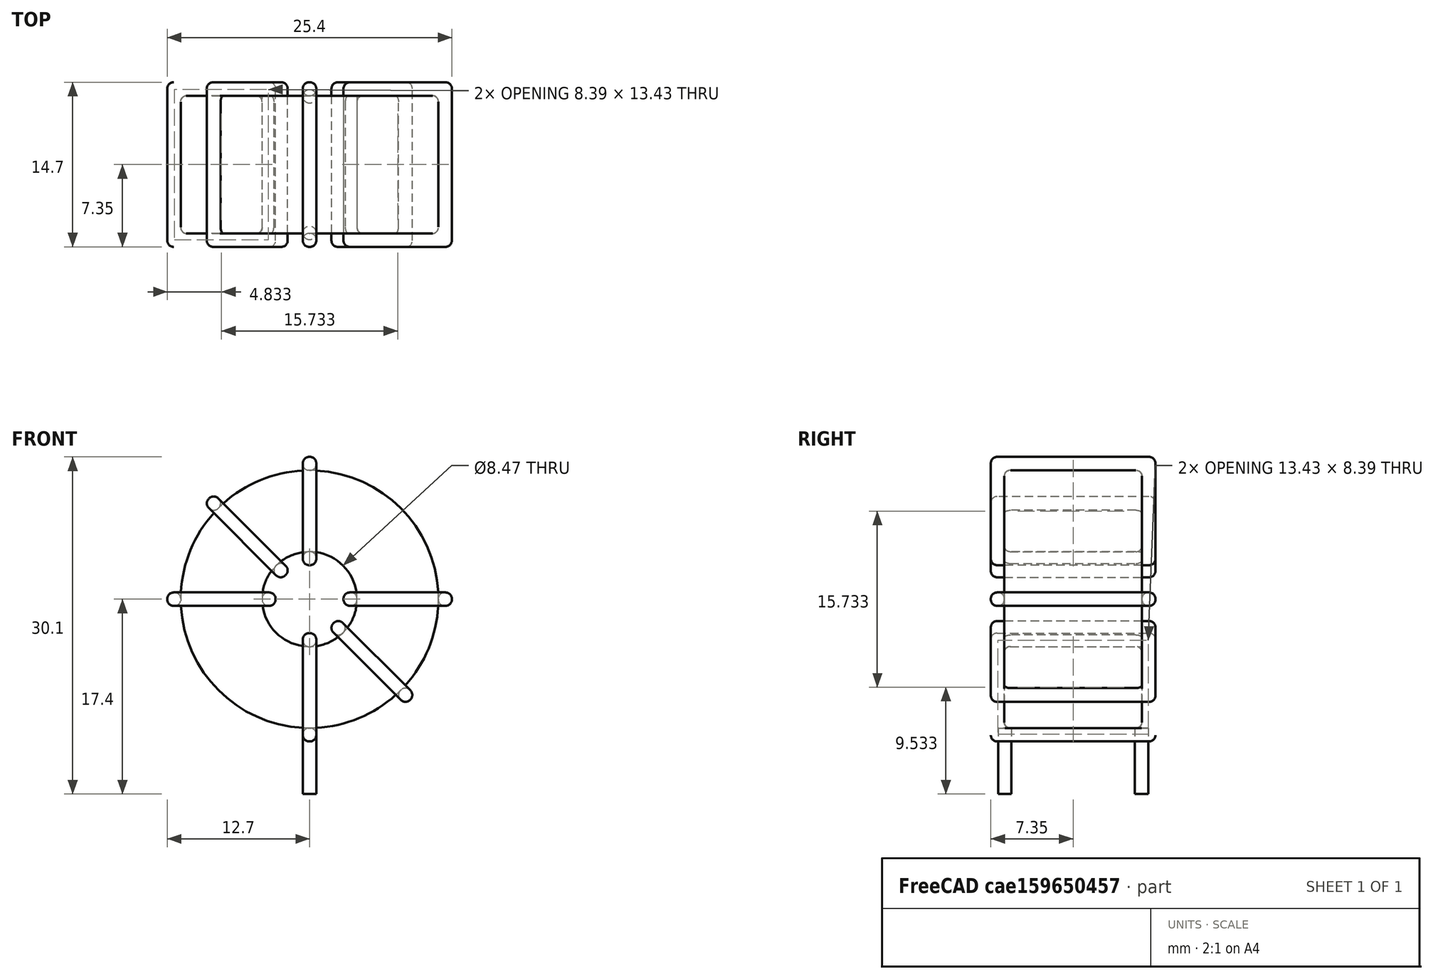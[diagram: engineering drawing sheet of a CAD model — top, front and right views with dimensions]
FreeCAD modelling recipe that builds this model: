
FCSTD DOCUMENT  (FreeCAD 0.16R6703 (Git))
Label: L_Toroid_Vertical_L25.4mm_W14.7mm_P12.20mm_Vishay_TJ5_BigPads
License: All rights reserved
LicenseURL: http://en.wikipedia.org/wiki/All_rights_reserved
objects: Sketcher::SketchObject×6, PartDesign::Pad×6, PartDesign::Fillet×5, Spreadsheet::Sheet×1
note: 23 computed .brp shape members not serialized (recipe doc carries the construction recipe); baked Part::Feature solids carry a one-line shape summary decoded from their .brp

FEATURE [Spreadsheet::Sheet] Spreadsheet  label="dimensions"
  cells = A1=Wx; B1(Wx)=25.4; C1(WW)=8.466666666666667; D1=25.4; A2=Wy; B2(Wy)=14.7; D2=14.7; A3=RM; B3(RMx)=12.2; C3(RMy)=0; A4=d_wire; B4(d_wire)=1.2; A5=H; B5(H)=25.4; A6=offsetx; B6(offsetx)=12.7
FEATURE [Sketcher::SketchObject] Sketch
  Placement = pos=(0,-6.1,0) rot=(1,0,0;1.5708rad)
  expr: Placement.Base.y = -Spreadsheet.RMx / 2
  expr: Constraints[0] = Spreadsheet.Wx / 2 - Spreadsheet.d_wire
  expr: Constraints[4] = Spreadsheet.WW / 2
  expr: Constraints[2] = Spreadsheet.Wx / 2 + Spreadsheet.d_wire + 0.5
  sketch-geometry (2):
    g0: Circle CenterX=0 CenterY=14.4 CenterZ=0 NormalX=0 NormalY=0 NormalZ=1 Radius=11.5
    g1: Circle CenterX=0 CenterY=14.4 CenterZ=0 NormalX=0 NormalY=0 NormalZ=1 Radius=4.23333
  constraints (5):
    c: Radius(g0) = 11.5
    c: DistanceX(g-1,g0) = 0
    c: DistanceY(g-1,g0) = 14.4
    c: Coincident(g1,g0)
    c: Radius(g1) = 4.23333
FEATURE [PartDesign::Pad] Pad
  Length = 12.3
  Length2 = 100
  Midplane = true
  Placement = pos=(0,-6.1,0) rot=(1,0,0;1.5708rad)
  Sketch = -> Sketch
  Type = 0
  expr: Length = Spreadsheet.Wy - 2 * Spreadsheet.d_wire
FEATURE [Sketcher::SketchObject] Sketch001
  Placement = pos=(0,0,1.7) rot=(0,0,1;0rad)
  expr: Placement.Base.z = 0.5 + Spreadsheet.d_wire
  expr: Constraints[4] = Spreadsheet.RMy
  expr: Constraints[2] = -Spreadsheet.RMx
  expr: Constraints[1] = Spreadsheet.d_wire / 2
  sketch-geometry (2):
    g0: Circle CenterX=0 CenterY=0 CenterZ=0 NormalX=0 NormalY=0 NormalZ=1 Radius=0.6
    g1: Circle CenterX=0 CenterY=-12.2 CenterZ=0 NormalX=0 NormalY=0 NormalZ=1 Radius=0.6
  constraints (5):
    c: Equal(g0,g1)
    c: Radius(g0) = 0.6
    c: DistanceY(g-1,g1) = -12.2
    c: Coincident(g0,g-1)
    c: DistanceX(g-1,g1) = 0
FEATURE [PartDesign::Pad] Pad001
  Length = 1.2
  Length2 = 4.7
  Placement = pos=(0,0,1.7) rot=(0,0,1;0rad)
  Reversed = true
  Sketch = -> Sketch001
  Type = 4
  expr: Length2 = 3.5 + Spreadsheet.d_wire
  expr: Length = Spreadsheet.d_wire
FEATURE [PartDesign::Fillet] Fillet
  Base = -> Pad [Edge6,Edge3,Edge2]
  Placement = pos=(0,-6.1,0) rot=(1,0,0;1.5708rad)
  Radius = 0.5
FEATURE [Sketcher::SketchObject] Sketch003
  Placement = pos=(0,1.25,14.4) rot=(1,0,0;3.14159rad)
  expr: Constraints[18] = Spreadsheet.d_wire
  expr: Constraints[16] = Spreadsheet.d_wire
  expr: Constraints[19] = Spreadsheet.d_wire
  expr: Constraints[17] = Spreadsheet.d_wire
  expr: Placement.Base.y = -1 * (Spreadsheet.RMx - Spreadsheet.Wy) / 2
  expr: Constraints[21] = (Spreadsheet.Wx - Spreadsheet.WW) / 2 - Spreadsheet.d_wire
  expr: Constraints[22] = Spreadsheet.Wx / 2 - Spreadsheet.d_wire
  expr: Constraints[43] = Spreadsheet.d_wire
  expr: Constraints[48] = Spreadsheet.Wx - Spreadsheet.d_wire * 2
  expr: Constraints[49] = Spreadsheet.Wy
  expr: Placement.Base.z = Spreadsheet.Wx / 2 + Spreadsheet.d_wire + 0.5
  sketch-geometry (16):
    g0: LineSegment StartX=-3.03333 StartY=0 StartZ=0 EndX=-12.7 EndY=0 EndZ=0
    g1: LineSegment StartX=-12.7 StartY=0 StartZ=0 EndX=-12.7 EndY=14.7 EndZ=0
    g2: LineSegment StartX=-12.7 StartY=14.7 StartZ=0 EndX=-3.03333 EndY=14.7 EndZ=0
    g3: LineSegment StartX=-3.03333 StartY=14.7 StartZ=0 EndX=-3.03333 EndY=0 EndZ=0
    g4: LineSegment StartX=-11.5 StartY=13.5 StartZ=0 EndX=-4.23333 EndY=13.5 EndZ=0
    g5: LineSegment StartX=-4.23333 StartY=13.5 StartZ=0 EndX=-4.23333 EndY=1.2 EndZ=0
    g6: LineSegment StartX=-4.23333 StartY=1.2 StartZ=0 EndX=-11.5 EndY=1.2 EndZ=0
    g7: LineSegment StartX=-11.5 StartY=1.2 StartZ=0 EndX=-11.5 EndY=13.5 EndZ=0
    g8: LineSegment StartX=3.03333 StartY=14.7 StartZ=0 EndX=12.7 EndY=14.7 EndZ=0
    g9: LineSegment StartX=12.7 StartY=14.7 StartZ=0 EndX=12.7 EndY=0 EndZ=0
    g10: LineSegment StartX=12.7 StartY=0 StartZ=0 EndX=3.03333 EndY=0 EndZ=0
    g11: LineSegment StartX=3.03333 StartY=0 StartZ=0 EndX=3.03333 EndY=14.7 EndZ=0
    g12: LineSegment StartX=4.23333 StartY=13.5 StartZ=0 EndX=11.5 EndY=13.5 EndZ=0
    g13: LineSegment StartX=11.5 StartY=13.5 StartZ=0 EndX=11.5 EndY=1.2 EndZ=0
    g14: LineSegment StartX=11.5 StartY=1.2 StartZ=0 EndX=4.23333 EndY=1.2 EndZ=0
    g15: LineSegment StartX=4.23333 StartY=1.2 StartZ=0 EndX=4.23333 EndY=13.5 EndZ=0
  constraints (50):
    c: Horizontal(g0)
    c: Coincident(g1,g0)
    c: Vertical(g1)
    c: Coincident(g2,g1)
    c: Horizontal(g2)
    c: Coincident(g3,g2)
    c: Coincident(g3,g0)
    c: Vertical(g3)
    c: Coincident(g4,g5)
    c: Coincident(g5,g6)
    c: Coincident(g6,g7)
    c: Coincident(g7,g4)
    c: Horizontal(g4)
    c: Horizontal(g6)
    c: Vertical(g5)
    c: Vertical(g7)
    c: DistanceX(g1,g4) = 1.2
    c: DistanceY(g4,g1) = 1.2
    c: DistanceX(g5,g0) = 1.2
    c: DistanceY(g0,g5) = 1.2
    c: DistanceY(g-1,g0) = 0
    c: DistanceX(g6,g6) = 7.26667
    c: DistanceX(g6,g-1) = 11.5
    c: Coincident(g8,g9)
    c: Coincident(g9,g10)
    c: Coincident(g10,g11)
    c: Coincident(g11,g8)
    c: Horizontal(g8)
    c: Horizontal(g10)
    c: Vertical(g9)
    c: Vertical(g11)
    c: Coincident(g12,g13)
    c: Coincident(g13,g14)
    c: Coincident(g14,g15)
    c: Coincident(g15,g12)
    c: Horizontal(g12)
    c: Horizontal(g14)
    c: Vertical(g13)
    c: Vertical(g15)
    c: DistanceY(g8,g2) = 0
    c: DistanceY(g10,g0) = 0
    c: DistanceY(g14,g5) = 0
    c: DistanceY(g12,g4) = 0
    c: DistanceX(g8,g12) = 1.2
    c: Equal(g8,g2)
    c: Equal(g12,g4)
    c: Equal(g9,g1)
    c: Equal(g13,g7)
    c: DistanceX(g4,g12) = 23
    c: DistanceY(g0,g1) = 14.7
FEATURE [PartDesign::Pad] Pad002
  Length = 1.2
  Length2 = 100
  Midplane = true
  Placement = pos=(0,1.25,14.4) rot=(1,0,0;3.14159rad)
  Sketch = -> Sketch003
  Type = 0
  expr: Length = Spreadsheet.d_wire
FEATURE [PartDesign::Fillet] Fillet001
  Base = -> Pad002 [Edge38,Edge41,Edge42,Edge43,Edge29,Edge32,Edge33,Edge34,Edge25,Edge35,Edge36,Edge13,Edge14,Edge15,Edge16,Edge17,Edge18,Edge19,Edge1,Edge2,Edge3,Edge4,Edge5,Edge6,Edge7,Edge37,Edge39,Edge40,Edge20,Edge23,Edge24,Edge21,Edge22,Edge8,Edge9,Edge10,Edge11,Edge12,Edge26,Edge27,+8 more]
  Placement = pos=(0,1.25,14.4) rot=(1,0,0;3.14159rad)
  Radius = 0.564
  expr: Radius = Spreadsheet.d_wire * 0.47
FEATURE [Sketcher::SketchObject] Sketch004
  Placement = pos=(0,1.25,14.4) rot=(0.92388,0,0.382683;3.14159rad)
  expr: Constraints[18] = Spreadsheet.d_wire
  expr: Constraints[16] = Spreadsheet.d_wire
  expr: Constraints[19] = Spreadsheet.d_wire
  expr: Constraints[17] = Spreadsheet.d_wire
  expr: Placement.Base.y = -1 * (Spreadsheet.RMx - Spreadsheet.Wy) / 2
  expr: Constraints[21] = (Spreadsheet.Wx - Spreadsheet.WW) / 2 - Spreadsheet.d_wire
  expr: Constraints[22] = Spreadsheet.Wx / 2 - Spreadsheet.d_wire
  expr: Constraints[43] = Spreadsheet.d_wire
  expr: Constraints[48] = Spreadsheet.Wx - 2 * Spreadsheet.d_wire
  expr: Constraints[49] = Spreadsheet.Wy
  expr: Placement.Base.z = Spreadsheet.Wx / 2 + Spreadsheet.d_wire + 0.5
  sketch-geometry (16):
    g0: LineSegment StartX=-3.03333 StartY=0 StartZ=0 EndX=-12.7 EndY=0 EndZ=0
    g1: LineSegment StartX=-12.7 StartY=0 StartZ=0 EndX=-12.7 EndY=14.7 EndZ=0
    g2: LineSegment StartX=-12.7 StartY=14.7 StartZ=0 EndX=-3.03333 EndY=14.7 EndZ=0
    g3: LineSegment StartX=-3.03333 StartY=14.7 StartZ=0 EndX=-3.03333 EndY=0 EndZ=0
    g4: LineSegment StartX=-11.5 StartY=13.5 StartZ=0 EndX=-4.23333 EndY=13.5 EndZ=0
    g5: LineSegment StartX=-4.23333 StartY=13.5 StartZ=0 EndX=-4.23333 EndY=1.2 EndZ=0
    g6: LineSegment StartX=-4.23333 StartY=1.2 StartZ=0 EndX=-11.5 EndY=1.2 EndZ=0
    g7: LineSegment StartX=-11.5 StartY=1.2 StartZ=0 EndX=-11.5 EndY=13.5 EndZ=0
    g8: LineSegment StartX=3.03333 StartY=14.7 StartZ=0 EndX=12.7 EndY=14.7 EndZ=0
    g9: LineSegment StartX=12.7 StartY=14.7 StartZ=0 EndX=12.7 EndY=0 EndZ=0
    g10: LineSegment StartX=12.7 StartY=0 StartZ=0 EndX=3.03333 EndY=0 EndZ=0
    g11: LineSegment StartX=3.03333 StartY=0 StartZ=0 EndX=3.03333 EndY=14.7 EndZ=0
    g12: LineSegment StartX=4.23333 StartY=13.5 StartZ=0 EndX=11.5 EndY=13.5 EndZ=0
    g13: LineSegment StartX=11.5 StartY=13.5 StartZ=0 EndX=11.5 EndY=1.2 EndZ=0
    g14: LineSegment StartX=11.5 StartY=1.2 StartZ=0 EndX=4.23333 EndY=1.2 EndZ=0
    g15: LineSegment StartX=4.23333 StartY=1.2 StartZ=0 EndX=4.23333 EndY=13.5 EndZ=0
  constraints (50):
    c: Horizontal(g0)
    c: Coincident(g1,g0)
    c: Vertical(g1)
    c: Coincident(g2,g1)
    c: Horizontal(g2)
    c: Coincident(g3,g2)
    c: Coincident(g3,g0)
    c: Vertical(g3)
    c: Coincident(g4,g5)
    c: Coincident(g5,g6)
    c: Coincident(g6,g7)
    c: Coincident(g7,g4)
    c: Horizontal(g4)
    c: Horizontal(g6)
    c: Vertical(g5)
    c: Vertical(g7)
    c: DistanceX(g1,g4) = 1.2
    c: DistanceY(g4,g1) = 1.2
    c: DistanceX(g5,g0) = 1.2
    c: DistanceY(g0,g5) = 1.2
    c: DistanceY(g-1,g0) = 0
    c: DistanceX(g6,g6) = 7.26667
    c: DistanceX(g6,g-1) = 11.5
    c: Coincident(g8,g9)
    c: Coincident(g9,g10)
    c: Coincident(g10,g11)
    c: Coincident(g11,g8)
    c: Horizontal(g8)
    c: Horizontal(g10)
    c: Vertical(g9)
    c: Vertical(g11)
    c: Coincident(g12,g13)
    c: Coincident(g13,g14)
    c: Coincident(g14,g15)
    c: Coincident(g15,g12)
    c: Horizontal(g12)
    c: Horizontal(g14)
    c: Vertical(g13)
    c: Vertical(g15)
    c: DistanceY(g8,g2) = 0
    c: DistanceY(g10,g0) = 0
    c: DistanceY(g14,g5) = 0
    c: DistanceY(g12,g4) = 0
    c: DistanceX(g8,g12) = 1.2
    c: Equal(g8,g2)
    c: Equal(g12,g4)
    c: Equal(g9,g1)
    c: Equal(g13,g7)
    c: DistanceX(g4,g12) = 23
    c: DistanceY(g0,g1) = 14.7
FEATURE [PartDesign::Pad] Pad003
  Length = 1.2
  Length2 = 100
  Midplane = true
  Placement = pos=(0,1.25,14.4) rot=(0.92388,0,0.382683;3.14159rad)
  Sketch = -> Sketch004
  Type = 0
  expr: Length = Spreadsheet.d_wire
FEATURE [PartDesign::Fillet] Fillet002
  Base = -> Pad003 [Edge38,Edge41,Edge42,Edge43,Edge29,Edge32,Edge33,Edge34,Edge25,Edge35,Edge36,Edge13,Edge14,Edge15,Edge16,Edge17,Edge18,Edge19,Edge1,Edge2,Edge3,Edge4,Edge5,Edge6,Edge7,Edge37,Edge39,Edge40,Edge20,Edge23,Edge24,Edge21,Edge22,Edge8,Edge9,Edge10,Edge11,Edge12,Edge26,Edge27,+8 more]
  Placement = pos=(0,1.25,14.4) rot=(0.92388,0,0.382683;3.14159rad)
  Radius = 0.564
  expr: Radius = Spreadsheet.d_wire * 0.47
FEATURE [Sketcher::SketchObject] Sketch005
  Placement = pos=(0,1.25,14.4) rot=(0.92388,0,-0.382683;3.14159rad)
  expr: Constraints[18] = Spreadsheet.d_wire
  expr: Constraints[16] = Spreadsheet.d_wire
  expr: Constraints[19] = Spreadsheet.d_wire
  expr: Constraints[17] = Spreadsheet.d_wire
  expr: Placement.Base.y = -1 * (Spreadsheet.RMx - Spreadsheet.Wy) / 2
  expr: Constraints[21] = (Spreadsheet.Wx - Spreadsheet.WW) / 2 - Spreadsheet.d_wire
  expr: Constraints[22] = Spreadsheet.Wx / 2 - Spreadsheet.d_wire
  expr: Constraints[43] = Spreadsheet.d_wire
  expr: Constraints[48] = Spreadsheet.Wx - 2 * Spreadsheet.d_wire
  expr: Constraints[49] = Spreadsheet.Wy
  expr: Placement.Base.z = Spreadsheet.Wx / 2 + Spreadsheet.d_wire + 0.5
  sketch-geometry (16):
    g0: LineSegment StartX=-3.03333 StartY=0 StartZ=0 EndX=-12.7 EndY=0 EndZ=0
    g1: LineSegment StartX=-12.7 StartY=0 StartZ=0 EndX=-12.7 EndY=14.7 EndZ=0
    g2: LineSegment StartX=-12.7 StartY=14.7 StartZ=0 EndX=-3.03333 EndY=14.7 EndZ=0
    g3: LineSegment StartX=-3.03333 StartY=14.7 StartZ=0 EndX=-3.03333 EndY=0 EndZ=0
    g4: LineSegment StartX=-11.5 StartY=13.5 StartZ=0 EndX=-4.23333 EndY=13.5 EndZ=0
    g5: LineSegment StartX=-4.23333 StartY=13.5 StartZ=0 EndX=-4.23333 EndY=1.2 EndZ=0
    g6: LineSegment StartX=-4.23333 StartY=1.2 StartZ=0 EndX=-11.5 EndY=1.2 EndZ=0
    g7: LineSegment StartX=-11.5 StartY=1.2 StartZ=0 EndX=-11.5 EndY=13.5 EndZ=0
    g8: LineSegment StartX=3.03333 StartY=14.7 StartZ=0 EndX=12.7 EndY=14.7 EndZ=0
    g9: LineSegment StartX=12.7 StartY=14.7 StartZ=0 EndX=12.7 EndY=0 EndZ=0
    g10: LineSegment StartX=12.7 StartY=0 StartZ=0 EndX=3.03333 EndY=0 EndZ=0
    g11: LineSegment StartX=3.03333 StartY=0 StartZ=0 EndX=3.03333 EndY=14.7 EndZ=0
    g12: LineSegment StartX=4.23333 StartY=13.5 StartZ=0 EndX=11.5 EndY=13.5 EndZ=0
    g13: LineSegment StartX=11.5 StartY=13.5 StartZ=0 EndX=11.5 EndY=1.2 EndZ=0
    g14: LineSegment StartX=11.5 StartY=1.2 StartZ=0 EndX=4.23333 EndY=1.2 EndZ=0
    g15: LineSegment StartX=4.23333 StartY=1.2 StartZ=0 EndX=4.23333 EndY=13.5 EndZ=0
  constraints (50):
    c: Horizontal(g0)
    c: Coincident(g1,g0)
    c: Vertical(g1)
    c: Coincident(g2,g1)
    c: Horizontal(g2)
    c: Coincident(g3,g2)
    c: Coincident(g3,g0)
    c: Vertical(g3)
    c: Coincident(g4,g5)
    c: Coincident(g5,g6)
    c: Coincident(g6,g7)
    c: Coincident(g7,g4)
    c: Horizontal(g4)
    c: Horizontal(g6)
    c: Vertical(g5)
    c: Vertical(g7)
    c: DistanceX(g1,g4) = 1.2
    c: DistanceY(g4,g1) = 1.2
    c: DistanceX(g5,g0) = 1.2
    c: DistanceY(g0,g5) = 1.2
    c: DistanceY(g-1,g0) = 0
    c: DistanceX(g6,g6) = 7.26667
    c: DistanceX(g6,g-1) = 11.5
    c: Coincident(g8,g9)
    c: Coincident(g9,g10)
    c: Coincident(g10,g11)
    c: Coincident(g11,g8)
    c: Horizontal(g8)
    c: Horizontal(g10)
    c: Vertical(g9)
    c: Vertical(g11)
    c: Coincident(g12,g13)
    c: Coincident(g13,g14)
    c: Coincident(g14,g15)
    c: Coincident(g15,g12)
    c: Horizontal(g12)
    c: Horizontal(g14)
    c: Vertical(g13)
    c: Vertical(g15)
    c: DistanceY(g8,g2) = 0
    c: DistanceY(g10,g0) = 0
    c: DistanceY(g14,g5) = 0
    c: DistanceY(g12,g4) = 0
    c: DistanceX(g8,g12) = 1.2
    c: Equal(g8,g2)
    c: Equal(g12,g4)
    c: Equal(g9,g1)
    c: Equal(g13,g7)
    c: DistanceX(g4,g12) = 23
    c: DistanceY(g0,g1) = 14.7
FEATURE [PartDesign::Pad] Pad004
  Length = 1.2
  Length2 = 100
  Midplane = true
  Placement = pos=(0,1.25,14.4) rot=(0.92388,0,-0.382683;3.14159rad)
  Sketch = -> Sketch005
  Type = 0
  expr: Length = Spreadsheet.d_wire
FEATURE [PartDesign::Fillet] Fillet003
  Base = -> Pad004 [Edge38,Edge41,Edge42,Edge43,Edge29,Edge32,Edge33,Edge34,Edge25,Edge35,Edge36,Edge13,Edge14,Edge15,Edge16,Edge17,Edge18,Edge19,Edge1,Edge2,Edge3,Edge4,Edge5,Edge6,Edge7,Edge37,Edge39,Edge40,Edge20,Edge23,Edge24,Edge21,Edge22,Edge8,Edge9,Edge10,Edge11,Edge12,Edge26,Edge27,+8 more]
  Placement = pos=(0,1.25,14.4) rot=(0.92388,0,-0.382683;3.14159rad)
  Radius = 0.564
  expr: Radius = Spreadsheet.d_wire * 0.47
FEATURE [Sketcher::SketchObject] Sketch006
  Placement = pos=(0,1.25,14.4) rot=(0.707107,0,0.707107;3.14159rad)
  expr: Constraints[18] = Spreadsheet.d_wire
  expr: Constraints[16] = Spreadsheet.d_wire
  expr: Constraints[19] = Spreadsheet.d_wire
  expr: Constraints[17] = Spreadsheet.d_wire
  expr: Placement.Base.y = -1 * (Spreadsheet.RMx - Spreadsheet.Wy) / 2
  expr: Constraints[21] = (Spreadsheet.Wx - Spreadsheet.WW) / 2 - Spreadsheet.d_wire
  expr: Constraints[22] = Spreadsheet.Wx / 2 - Spreadsheet.d_wire
  expr: Constraints[43] = Spreadsheet.d_wire
  expr: Constraints[48] = Spreadsheet.Wx - Spreadsheet.d_wire * 2
  expr: Constraints[49] = Spreadsheet.Wy
  expr: Placement.Base.z = Spreadsheet.Wx / 2 + Spreadsheet.d_wire + 0.5
  sketch-geometry (16):
    g0: LineSegment StartX=-3.03333 StartY=0 StartZ=0 EndX=-12.7 EndY=0 EndZ=0
    g1: LineSegment StartX=-12.7 StartY=0 StartZ=0 EndX=-12.7 EndY=14.7 EndZ=0
    g2: LineSegment StartX=-12.7 StartY=14.7 StartZ=0 EndX=-3.03333 EndY=14.7 EndZ=0
    g3: LineSegment StartX=-3.03333 StartY=14.7 StartZ=0 EndX=-3.03333 EndY=0 EndZ=0
    g4: LineSegment StartX=-11.5 StartY=13.5 StartZ=0 EndX=-4.23333 EndY=13.5 EndZ=0
    g5: LineSegment StartX=-4.23333 StartY=13.5 StartZ=0 EndX=-4.23333 EndY=1.2 EndZ=0
    g6: LineSegment StartX=-4.23333 StartY=1.2 StartZ=0 EndX=-11.5 EndY=1.2 EndZ=0
    g7: LineSegment StartX=-11.5 StartY=1.2 StartZ=0 EndX=-11.5 EndY=13.5 EndZ=0
    g8: LineSegment StartX=3.03333 StartY=14.7 StartZ=0 EndX=12.7 EndY=14.7 EndZ=0
    g9: LineSegment StartX=12.7 StartY=14.7 StartZ=0 EndX=12.7 EndY=0 EndZ=0
    g10: LineSegment StartX=12.7 StartY=0 StartZ=0 EndX=3.03333 EndY=0 EndZ=0
    g11: LineSegment StartX=3.03333 StartY=0 StartZ=0 EndX=3.03333 EndY=14.7 EndZ=0
    g12: LineSegment StartX=4.23333 StartY=13.5 StartZ=0 EndX=11.5 EndY=13.5 EndZ=0
    g13: LineSegment StartX=11.5 StartY=13.5 StartZ=0 EndX=11.5 EndY=1.2 EndZ=0
    g14: LineSegment StartX=11.5 StartY=1.2 StartZ=0 EndX=4.23333 EndY=1.2 EndZ=0
    g15: LineSegment StartX=4.23333 StartY=1.2 StartZ=0 EndX=4.23333 EndY=13.5 EndZ=0
  constraints (50):
    c: Horizontal(g0)
    c: Coincident(g1,g0)
    c: Vertical(g1)
    c: Coincident(g2,g1)
    c: Horizontal(g2)
    c: Coincident(g3,g2)
    c: Coincident(g3,g0)
    c: Vertical(g3)
    c: Coincident(g4,g5)
    c: Coincident(g5,g6)
    c: Coincident(g6,g7)
    c: Coincident(g7,g4)
    c: Horizontal(g4)
    c: Horizontal(g6)
    c: Vertical(g5)
    c: Vertical(g7)
    c: DistanceX(g1,g4) = 1.2
    c: DistanceY(g4,g1) = 1.2
    c: DistanceX(g5,g0) = 1.2
    c: DistanceY(g0,g5) = 1.2
    c: DistanceY(g-1,g0) = 0
    c: DistanceX(g6,g6) = 7.26667
    c: DistanceX(g6,g-1) = 11.5
    c: Coincident(g8,g9)
    c: Coincident(g9,g10)
    c: Coincident(g10,g11)
    c: Coincident(g11,g8)
    c: Horizontal(g8)
    c: Horizontal(g10)
    c: Vertical(g9)
    c: Vertical(g11)
    c: Coincident(g12,g13)
    c: Coincident(g13,g14)
    c: Coincident(g14,g15)
    c: Coincident(g15,g12)
    c: Horizontal(g12)
    c: Horizontal(g14)
    c: Vertical(g13)
    c: Vertical(g15)
    c: DistanceY(g8,g2) = 0
    c: DistanceY(g10,g0) = 0
    c: DistanceY(g14,g5) = 0
    c: DistanceY(g12,g4) = 0
    c: DistanceX(g8,g12) = 1.2
    c: Equal(g8,g2)
    c: Equal(g12,g4)
    c: Equal(g9,g1)
    c: Equal(g13,g7)
    c: DistanceX(g4,g12) = 23
    c: DistanceY(g0,g1) = 14.7
FEATURE [PartDesign::Pad] Pad005
  Length = 1.2
  Length2 = 100
  Midplane = true
  Placement = pos=(0,1.25,14.4) rot=(0.707107,0,0.707107;3.14159rad)
  Sketch = -> Sketch006
  Type = 0
  expr: Length = Spreadsheet.d_wire
FEATURE [PartDesign::Fillet] Fillet004
  Base = -> Pad005 [Edge38,Edge41,Edge42,Edge43,Edge29,Edge32,Edge33,Edge34,Edge25,Edge35,Edge36,Edge13,Edge14,Edge15,Edge16,Edge17,Edge18,Edge19,Edge1,Edge2,Edge3,Edge4,Edge5,Edge6,Edge7,Edge37,Edge39,Edge40,Edge20,Edge23,Edge24,Edge21,Edge22,Edge8,Edge9,Edge10,Edge11,Edge12,Edge26,Edge27,+8 more]
  Placement = pos=(0,1.25,14.4) rot=(0.707107,0,0.707107;3.14159rad)
  Radius = 0.564
  expr: Radius = Spreadsheet.d_wire * 0.47
